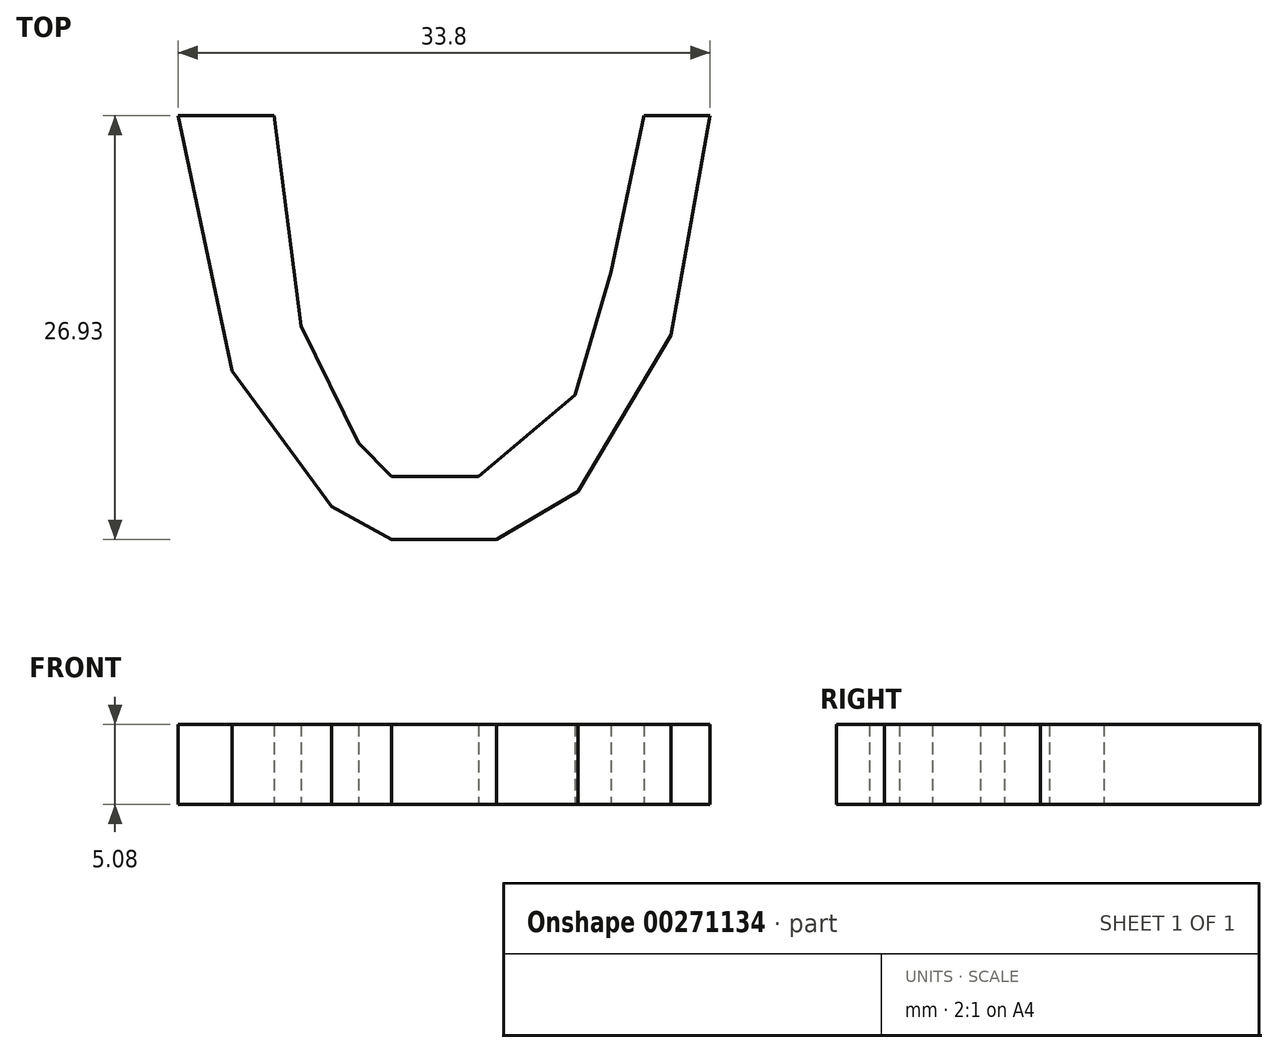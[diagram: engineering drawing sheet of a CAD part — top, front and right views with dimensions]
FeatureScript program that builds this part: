
annotation { "Feature Type Name" : "Feature", "Feature Type Description" : "" }
export const myFeature = defineFeature(function(context is Context, id is Id, definition is map)
    precondition{}
    {
        {
            var Q0;
            Q0=qCreatedBy(makeId("Top.planeOp"),FACE);
            var sketch = newSketch(context, id + "F0", { "sketchPlane" : qUnion([Q0])});
            skLineSegment(sketch, "E0", {"start": v(-32.84, 37.43) * mm, "end": v(-28.64, 37.43) * mm});
            skLineSegment(sketch, "E1", {"start": v(-28.64, 37.43) * mm, "end": v(-31.13, 23.49) * mm});
            skLineSegment(sketch, "E2", {"start": v(-31.13, 23.49) * mm, "end": v(-37.04, 13.56) * mm});
            skLineSegment(sketch, "E3", {"start": v(-37.04, 13.56) * mm, "end": v(-42.2, 10.5) * mm});
            skLineSegment(sketch, "E4", {"start": v(-42.2, 10.5) * mm, "end": v(-48.88, 10.5) * mm});
            skLineSegment(sketch, "E5", {"start": v(-48.88, 10.5) * mm, "end": v(-52.7, 12.6) * mm});
            skLineSegment(sketch, "E6", {"start": v(-52.7, 12.6) * mm, "end": v(-59, 21.2) * mm});
            skLineSegment(sketch, "E7", {"start": v(-59, 21.2) * mm, "end": v(-62.44, 37.43) * mm});
            skLineSegment(sketch, "E8", {"start": v(-62.44, 37.43) * mm, "end": v(-56.33, 37.43) * mm});
            skLineSegment(sketch, "E9", {"start": v(-56.33, 37.43) * mm, "end": v(-54.61, 24.06) * mm});
            skLineSegment(sketch, "E10", {"start": v(-54.61, 24.06) * mm, "end": v(-50.98, 16.61) * mm});
            skLineSegment(sketch, "E11", {"start": v(-50.98, 16.61) * mm, "end": v(-48.88, 14.51) * mm});
            skLineSegment(sketch, "E12", {"start": v(-48.88, 14.51) * mm, "end": v(-43.35, 14.51) * mm});
            skLineSegment(sketch, "E13", {"start": v(-43.35, 14.51) * mm, "end": v(-37.24, 19.67) * mm});
            skLineSegment(sketch, "E14", {"start": v(-37.24, 19.67) * mm, "end": v(-34.94, 27.5) * mm});
            skLineSegment(sketch, "E15", {"start": v(-34.94, 27.5) * mm, "end": v(-32.84, 37.43) * mm});
            skPoint(sketch, "E16.orphan", {"position": v(-37.04, 37.43) * mm});
            skSolve(sketch);
        }
        {
            var Q0;
            Q0 = qSketchRegion(id + "F0", true);
            extrude(context, id + "F1", {"entities" : qUnion([Q0]), "depth" : 5.08 * mm});
        }
    });
